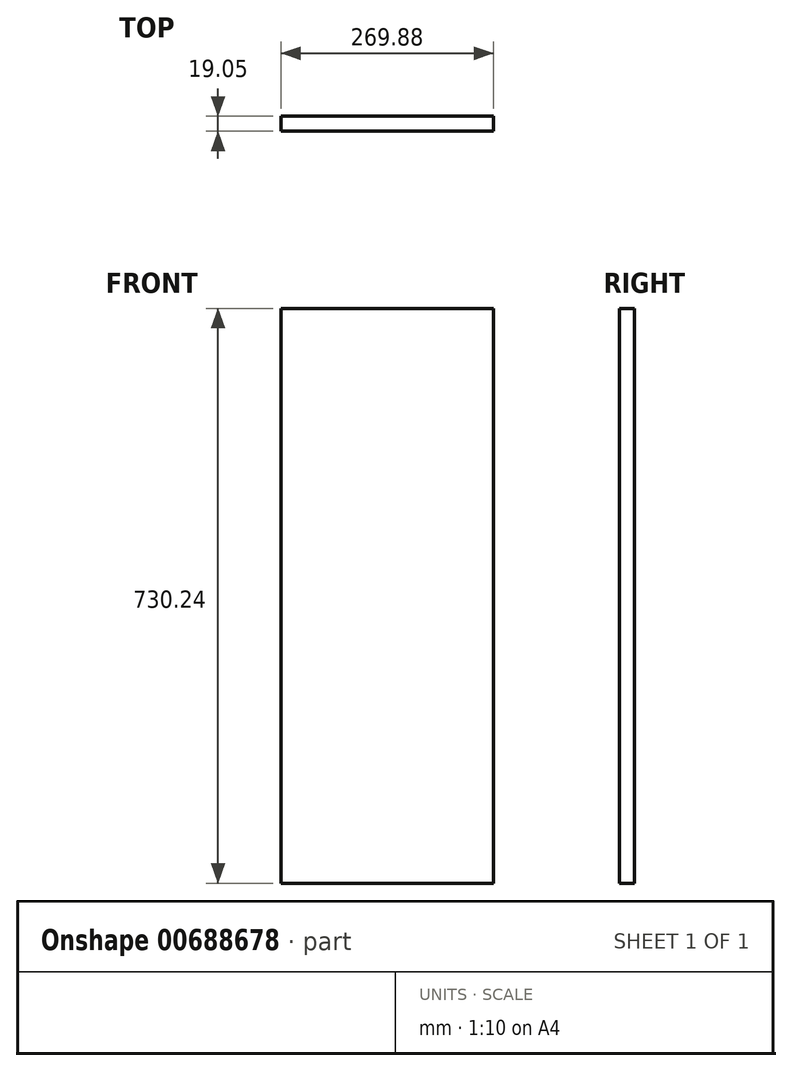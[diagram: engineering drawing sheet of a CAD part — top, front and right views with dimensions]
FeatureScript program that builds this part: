
annotation { "Feature Type Name" : "Feature", "Feature Type Description" : "" }
export const myFeature = defineFeature(function(context is Context, id is Id, definition is map)
    precondition{}
    {
        {
            var Q0;
            Q0=qCreatedBy(makeId("Front.planeOp"),FACE);
            var sketch = newSketch(context, id + "F0", { "sketchPlane" : qUnion([Q0])});
            skLineSegment(sketch, "E0.bottom", {"start": v(134.94, 365.12) * mm, "end": v(-134.94, 365.12) * mm});
            skLineSegment(sketch, "E0.top", {"start": v(134.94, -365.13) * mm, "end": v(-134.94, -365.13) * mm});
            skLineSegment(sketch, "E0.left", {"start": v(134.94, 365.12) * mm, "end": v(134.94, -365.13) * mm});
            skLineSegment(sketch, "E0.right", {"start": v(-134.94, 365.12) * mm, "end": v(-134.94, -365.13) * mm});
            skPoint(sketch, "E0.middle", {"position": v(0, 0) * mm});
            skSolve(sketch);
        }
        {
            var Q0;
            Q0=makeQuery(id+"F0.imprint","IMPRINT",FACE,{"disambiguationData":[TD([[makeQuery(id+"F0.imprint","IMPRINT",EDGE,{"derivedFrom":sQuery(id+"F0.wireOp",EDGE,"E0.bottom")}),1.0]])]});
            extrude(context, id + "F1", {"entities" : qUnion([Q0]), "depth" : 19.05 * mm, "offsetDistance" : 25.4 * mm});
        }
    });
